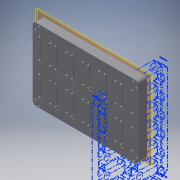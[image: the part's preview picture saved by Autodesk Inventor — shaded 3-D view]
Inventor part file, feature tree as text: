
AUTODESK INVENTOR PART (.ipt)
format: ipt  version: 2019.4 (Build 234330000, 330)  size: 360,960 bytes
history: native  units: mm
features: reference x8, other x5, extrude x3, sketch x3, plane x2, projected_geometry x2, pattern_linear x1, shell x1
ambient origin geometry x8: Origin, YZ Plane, XZ Plane, XY Plane, X Axis, Y Axis, Z Axis, Center Point
bodies: Solid1 (feature_tree)
feature tree (25):
  plane  "Work Plane1"
  plane  "Work Plane2"
  extrude  "Extrusion1"  Depth=4.0mm TaperAngle=0.0deg
  extrude  "Extrusion2"  Depth=2.9mm
  extrude  "Extrusion3"  Depth=18.0mm
  pattern_linear  "Rectangular Pattern2"  Spacing1=0.2mm  [1 undecoded]
  shell  "Shell2"  Thickness=0.2mm
  sketch  "Sketch2"  dims[d0=9.3mm d1=0.0mm d3=4.0mm d4=0.0mm]
  reference  "Reference1"
  sketch  "Sketch3"  dims[d7=2.9mm d8=2.9mm]
  projected_geometry  "Projected Loop1"
  reference  "Reference2"
  reference  "Reference3"
  reference  "Reference4"
  reference  "Reference5"
  reference  "Reference6"
  sketch  "Sketch4"  dims[d19=1.0mm d20=0.0mm d21=60.0mm d23=18.0mm d24=20.0mm d26=36.0mm d35=0.2mm d36=0.2mm d37=0.2mm d39=2.9mm d40=2.9mm d41=2.9mm d42=1.0mm]
  reference  "Reference7"
  reference  "Reference8"
  projected_geometry  "Projected Loop3"
  other  "Full_HITscope_v0.iam"
  other  "05_Omniscope_base_v1:1"
  other  "Assembly_Omniscope_v1:11"
  other  "02_Camera_Lid:1"
  other  "00_electricpin_2.54_10x:2"
note: 1 required parameter value undecoded (feature->parameter linkage not recoverable at this tier; creation-order binding heuristic only, values carry confidence <= 0.55)
